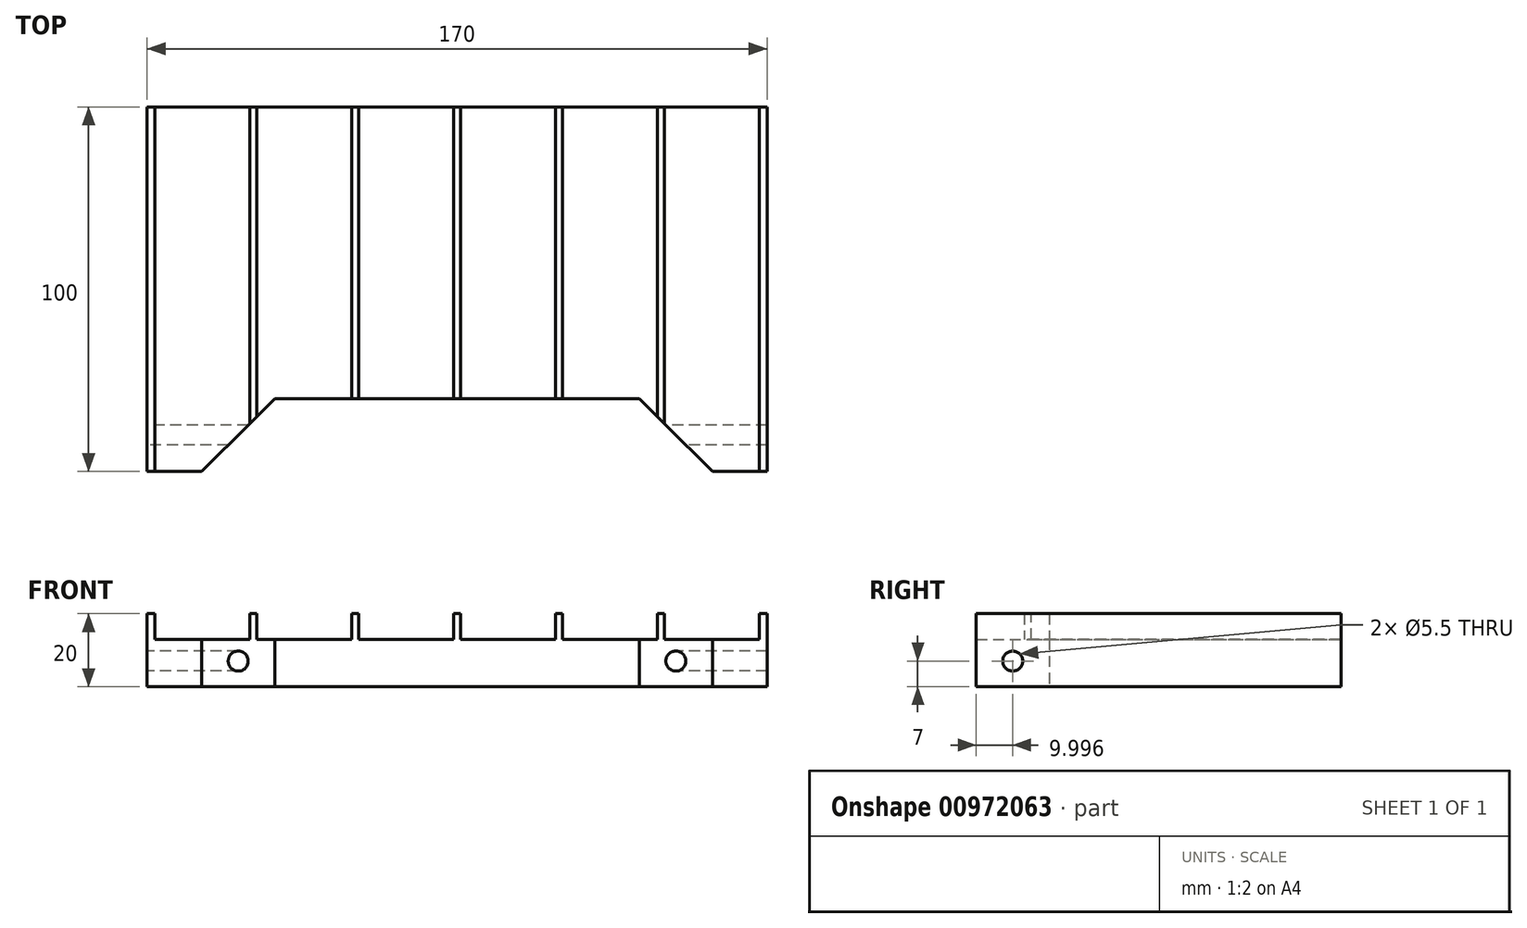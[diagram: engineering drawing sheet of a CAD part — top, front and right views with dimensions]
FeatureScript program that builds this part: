
annotation { "Feature Type Name" : "Feature", "Feature Type Description" : "" }
export const myFeature = defineFeature(function(context is Context, id is Id, definition is map)
    precondition{}
    {
        {
            var Q0;
            Q0=qCreatedBy(makeId("Top.planeOp"),FACE);
            var sketch = newSketch(context, id + "F0", { "sketchPlane" : qUnion([Q0])});
            skLineSegment(sketch, "E0", {"start": v(-34.97, -24.74) * mm, "end": v(-19.97, -24.74) * mm});
            skLineSegment(sketch, "E1", {"start": v(-19.97, -24.74) * mm, "end": v(0.03, -4.74) * mm});
            skLineSegment(sketch, "E2", {"start": v(0.03, -4.74) * mm, "end": v(100.03, -4.74) * mm});
            skLineSegment(sketch, "E3", {"start": v(100.03, -4.74) * mm, "end": v(120.03, -24.74) * mm});
            skLineSegment(sketch, "E4", {"start": v(120.03, -24.74) * mm, "end": v(135.03, -24.74) * mm});
            skLineSegment(sketch, "E5", {"start": v(-34.97, -24.74) * mm, "end": v(-34.97, 75.26) * mm});
            skLineSegment(sketch, "E6", {"start": v(-34.97, 75.26) * mm, "end": v(135.03, 75.26) * mm});
            skLineSegment(sketch, "E7", {"start": v(135.03, 75.26) * mm, "end": v(135.03, -24.74) * mm});
            skSolve(sketch);
        }
        {
            var Q0;
            Q0=makeQuery(id+"F0.imprint","IMPRINT",FACE,{"disambiguationData":[TD([[makeQuery(id+"F0.imprint","IMPRINT",EDGE,{"derivedFrom":sQuery(id+"F0.wireOp",EDGE,"E0")}),1.0]])]});
            extrude(context, id + "F1", {"entities" : qUnion([Q0]), "depth" : 20 * mm, "offsetDistance" : 25 * mm});
        }
        {
            var Q0;
            Q0=makeQuery(id+"F1.opExtrude","CAP_FACE",FACE,{"disambiguationData":[OSD([sQuery(id+"F0.wireOp",EDGE,"E0"),sQuery(id+"F0.wireOp",EDGE,"E1"),sQuery(id+"F0.wireOp",EDGE,"E2"),sQuery(id+"F0.wireOp",EDGE,"E3"),sQuery(id+"F0.wireOp",EDGE,"E4"),sQuery(id+"F0.wireOp",EDGE,"E5"),sQuery(id+"F0.wireOp",EDGE,"E6"),sQuery(id+"F0.wireOp",EDGE,"E7")])],"isStart":false});
            var sketch = newSketch(context, id + "F2", { "sketchPlane" : qUnion([Q0])});
            skLineSegment(sketch, "E8", {"start": v(-32.82, 82.66) * mm, "end": v(-32.82, -30.54) * mm});
            skLineSegment(sketch, "E9", {"start": v(-32.82, -30.54) * mm, "end": v(-6.82, -30.54) * mm});
            skLineSegment(sketch, "E10", {"start": v(-6.82, -30.54) * mm, "end": v(-6.82, 82.66) * mm});
            skLineSegment(sketch, "E11", {"start": v(-6.82, 82.66) * mm, "end": v(-32.82, 82.66) * mm});
            skLineSegment(sketch, "E12.1.0.0", {"start": v(-4.88, 82.66) * mm, "end": v(-4.88, -30.54) * mm});
            skLineSegment(sketch, "E12.1.0.1", {"start": v(21.12, -30.54) * mm, "end": v(21.12, 82.66) * mm});
            skLineSegment(sketch, "E12.1.0.2", {"start": v(21.12, 82.66) * mm, "end": v(-4.88, 82.66) * mm});
            skLineSegment(sketch, "E12.1.0.3", {"start": v(-4.88, -30.54) * mm, "end": v(21.12, -30.54) * mm});
            skLineSegment(sketch, "E12.2.0.0", {"start": v(23.06, 82.66) * mm, "end": v(23.06, -30.54) * mm});
            skLineSegment(sketch, "E12.2.0.1", {"start": v(49.06, -30.54) * mm, "end": v(49.06, 82.66) * mm});
            skLineSegment(sketch, "E12.2.0.2", {"start": v(49.06, 82.66) * mm, "end": v(23.06, 82.66) * mm});
            skLineSegment(sketch, "E12.2.0.3", {"start": v(23.06, -30.54) * mm, "end": v(49.06, -30.54) * mm});
            skLineSegment(sketch, "E12.3.0.0", {"start": v(51, 82.66) * mm, "end": v(51, -30.54) * mm});
            skLineSegment(sketch, "E12.3.0.1", {"start": v(77, -30.54) * mm, "end": v(77, 82.66) * mm});
            skLineSegment(sketch, "E12.3.0.2", {"start": v(77, 82.66) * mm, "end": v(51, 82.66) * mm});
            skLineSegment(sketch, "E12.3.0.3", {"start": v(51, -30.54) * mm, "end": v(77, -30.54) * mm});
            skLineSegment(sketch, "E12.4.0.0", {"start": v(78.94, 82.66) * mm, "end": v(78.94, -30.54) * mm});
            skLineSegment(sketch, "E12.4.0.1", {"start": v(104.94, -30.54) * mm, "end": v(104.94, 82.66) * mm});
            skLineSegment(sketch, "E12.4.0.2", {"start": v(104.94, 82.66) * mm, "end": v(78.94, 82.66) * mm});
            skLineSegment(sketch, "E12.4.0.3", {"start": v(78.94, -30.54) * mm, "end": v(104.94, -30.54) * mm});
            skLineSegment(sketch, "E12.5.0.0", {"start": v(106.88, 82.66) * mm, "end": v(106.88, -30.54) * mm});
            skLineSegment(sketch, "E12.5.0.1", {"start": v(132.88, -30.54) * mm, "end": v(132.88, 82.66) * mm});
            skLineSegment(sketch, "E12.5.0.2", {"start": v(132.88, 82.66) * mm, "end": v(106.88, 82.66) * mm});
            skLineSegment(sketch, "E12.5.0.3", {"start": v(106.88, -30.54) * mm, "end": v(132.88, -30.54) * mm});
            skLineSegment(sketch, "E12.direction1", {"start": v(-32.82, -30.54) * mm, "end": v(-4.88, -30.54) * mm, "construction": true});
            skSolve(sketch);
        }
        {
            var Q0;
            Q0 = qSketchRegion(id + "F2", true);
            extrude(context, id + "F3", {"entities" : qUnion([Q0]), "operationType" : NewBodyOperationType.REMOVE, "oppositeDirection" : true, "depth" : 7 * mm, "offsetDistance" : 25 * mm});
        }
        {
            var Q0;
            Q0=makeQuery(id+"F1.opExtrude","SWEPT_FACE",FACE,{"disambiguationData":[OSD([sQuery(id+"F0.wireOp",EDGE,"E5")])]});
            var sketch = newSketch(context, id + "F4", { "sketchPlane" : qUnion([Q0])});
            skCircle(sketch, "E13", {"center": v(14.74, 7) * mm, "radius": 2.75 * mm});
            skSolve(sketch);
        }
        {
            var Q0;
            Q0=makeQuery(id+"F4.imprint","IMPRINT",FACE,{"disambiguationData":[TD([[makeQuery(id+"F4.imprint","IMPRINT",EDGE,{"derivedFrom":sQuery(id+"F4.wireOp",EDGE,"E13")}),1.0]])]});
            var Q1;
            Q1=makeQuery(id+"F1.opExtrude","SWEPT_FACE",FACE,{"disambiguationData":[OSD([sQuery(id+"F0.wireOp",EDGE,"E7")])]});
            extrude(context, id + "F5", {"entities" : qUnion([Q0]), "operationType" : NewBodyOperationType.REMOVE, "endBound" : BoundingType.UP_TO_SURFACE, "oppositeDirection" : true, "depth" : 25 * mm, "endBoundEntityFace" : qUnion([Q1]), "offsetDistance" : 25 * mm});
        }
    });
